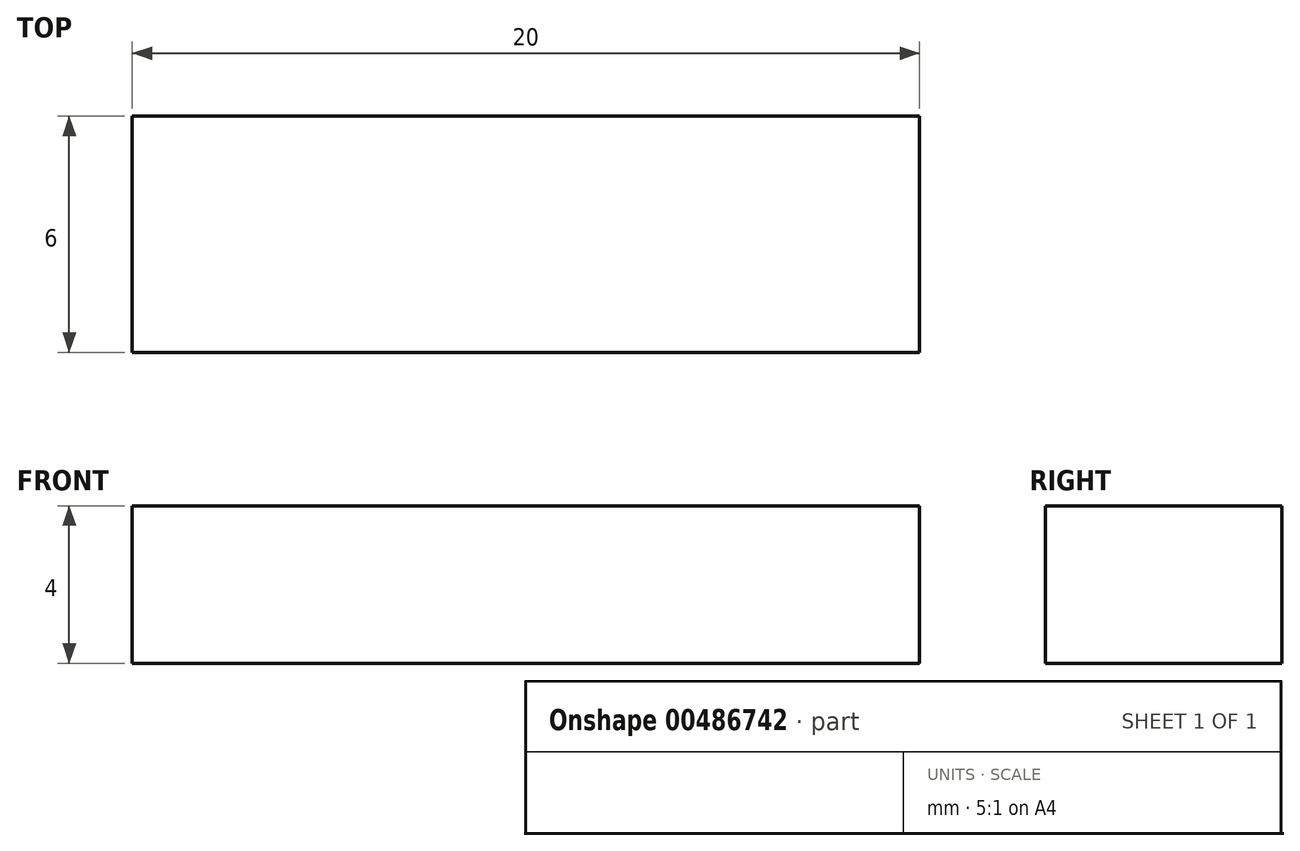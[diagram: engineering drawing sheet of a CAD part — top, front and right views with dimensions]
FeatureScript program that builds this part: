
annotation { "Feature Type Name" : "Feature", "Feature Type Description" : "" }
export const myFeature = defineFeature(function(context is Context, id is Id, definition is map)
    precondition{}
    {
        {
            var Q0;
            Q0=qCreatedBy(makeId("Top.planeOp"),FACE);
            var sketch = newSketch(context, id + "F0", { "sketchPlane" : qUnion([Q0])});
            skLineSegment(sketch, "E0.bottom", {"start": v(0, 0) * mm, "end": v(20, 0) * mm});
            skLineSegment(sketch, "E0.top", {"start": v(0, 6) * mm, "end": v(20, 6) * mm});
            skLineSegment(sketch, "E0.left", {"start": v(0, 0) * mm, "end": v(0, 6) * mm});
            skLineSegment(sketch, "E0.right", {"start": v(20, 0) * mm, "end": v(20, 6) * mm});
            skSolve(sketch);
        }
        {
            var Q0;
            Q0 = qSketchRegion(id + "F0", true);
            extrude(context, id + "F1", {"entities" : qUnion([Q0]), "depth" : 4 * mm});
        }
    });
